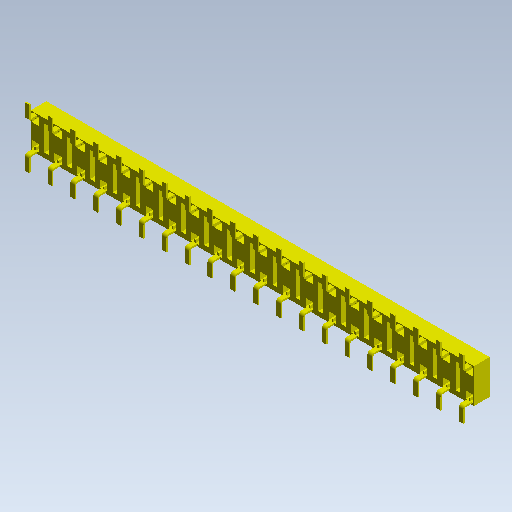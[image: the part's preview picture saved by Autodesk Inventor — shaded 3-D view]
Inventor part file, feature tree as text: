
AUTODESK INVENTOR PART (.ipt)
format: ipt  version: 2021 (Build 250183000, 183)  size: 902,144 bytes
history: native  units: mm (DEFAULTED — no unit token found)
features: other x7, extrude x4, sketch x4
ambient origin geometry x8: Origin, YZ Plane, XZ Plane, XY Plane, X Axis, Y Axis, Z Axis, Center Point
bodies: Solid1 (feature_tree)
feature tree (15):
  extrude  "Extrusion1"  Depth=49.276mm TaperAngle=0.0deg
  extrude  "Extrusion2"  Depth=10.16mm TaperAngle=0.0deg
  extrude  "Extrusion3"  [1 undecoded]
  extrude  "Extrusion4"  [1 undecoded]
  other  "pins_to_socket_XY"
  other  "pins_to_socket_YZ"
  other  "pins_to_socket_ZX"
  other  "pins_to_socket_X"
  other  "pins_to_socket_Y"
  other  "pins_to_socket_Z"
  other  "pins_to_socket_Center"
  sketch  "Sketch_11"  dims[d4=49.276mm d5=0.0mm d6=10.16mm d7=0.0mm]
  sketch  "Sketch_12"
  sketch  "Sketch_13"
  sketch  "Sketch_5"  dims[d0=1.7526mm d1=0.0mm d2=49.276mm d3=0.0mm]
note: 2 required parameter values undecoded (feature->parameter linkage not recoverable at this tier; creation-order binding heuristic only, values carry confidence <= 0.55)
